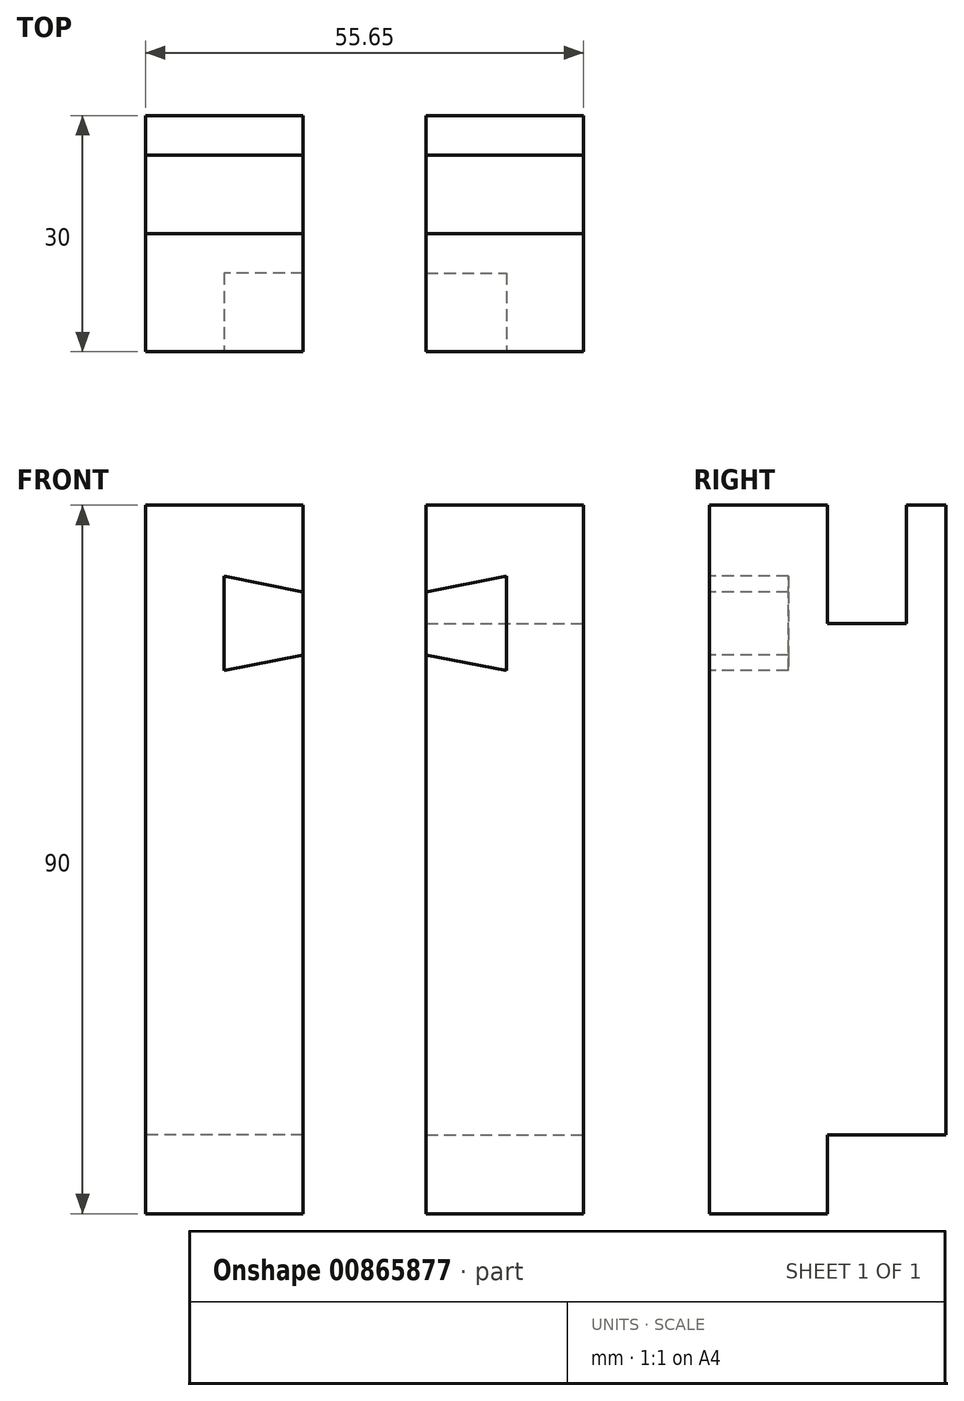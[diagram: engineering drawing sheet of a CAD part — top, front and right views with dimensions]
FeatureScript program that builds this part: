
annotation { "Feature Type Name" : "Feature", "Feature Type Description" : "" }
export const myFeature = defineFeature(function(context is Context, id is Id, definition is map)
    precondition{}
    {
        {
            var Q0;
            Q0=qCreatedBy(makeId("Top.planeOp"),FACE);
            var sketch = newSketch(context, id + "F0", { "sketchPlane" : qUnion([Q0])});
            skLineSegment(sketch, "E0.bottom", {"start": v(0, 0) * mm, "end": v(-20, 0) * mm});
            skLineSegment(sketch, "E0.top", {"start": v(0, 30) * mm, "end": v(-20, 30) * mm});
            skLineSegment(sketch, "E0.left", {"start": v(0, 0) * mm, "end": v(0, 30) * mm});
            skLineSegment(sketch, "E0.right", {"start": v(-20, 0) * mm, "end": v(-20, 30) * mm});
            skSolve(sketch);
        }
        {
            var Q0;
            Q0 = qSketchRegion(id + "F0", true);
            extrude(context, id + "F1", {"entities" : qUnion([Q0]), "depth" : 90 * mm, "offsetDistance" : 25 * mm});
        }
        {
            var Q0;
            Q0=makeQuery(id+"F1.opExtrude","CAP_FACE",FACE,{"disambiguationData":[OSD([sQuery(id+"F0.wireOp",EDGE,"E0.bottom"),sQuery(id+"F0.wireOp",EDGE,"E0.top"),sQuery(id+"F0.wireOp",EDGE,"E0.left"),sQuery(id+"F0.wireOp",EDGE,"E0.right")])],"isStart":false});
            var sketch = newSketch(context, id + "F2", { "sketchPlane" : qUnion([Q0])});
            skLineSegment(sketch, "E1.bottom", {"start": v(0, 15) * mm, "end": v(-20, 15) * mm});
            skLineSegment(sketch, "E1.top", {"start": v(0, 25) * mm, "end": v(-20, 25) * mm});
            skLineSegment(sketch, "E1.left", {"start": v(0, 15) * mm, "end": v(0, 25) * mm});
            skLineSegment(sketch, "E1.right", {"start": v(-20, 15) * mm, "end": v(-20, 25) * mm});
            skSolve(sketch);
        }
        {
            var Q0;
            Q0 = qSketchRegion(id + "F2", true);
            extrude(context, id + "F3", {"entities" : qUnion([Q0]), "operationType" : NewBodyOperationType.REMOVE, "oppositeDirection" : true, "depth" : 15 * mm, "offsetDistance" : 25 * mm});
        }
        {
            var Q0;
            Q0=makeQuery(id+"F1.opExtrude","CAP_FACE",FACE,{"disambiguationData":[OSD([sQuery(id+"F0.wireOp",EDGE,"E0.bottom"),sQuery(id+"F0.wireOp",EDGE,"E0.top"),sQuery(id+"F0.wireOp",EDGE,"E0.left"),sQuery(id+"F0.wireOp",EDGE,"E0.right")])],"isStart":true});
            var sketch = newSketch(context, id + "F4", { "sketchPlane" : qUnion([Q0])});
            skLineSegment(sketch, "E2.bottom", {"start": v(0, -30) * mm, "end": v(-20, -30) * mm});
            skLineSegment(sketch, "E2.top", {"start": v(0, -15) * mm, "end": v(-20, -15) * mm});
            skLineSegment(sketch, "E2.left", {"start": v(0, -30) * mm, "end": v(0, -15) * mm});
            skLineSegment(sketch, "E2.right", {"start": v(-20, -30) * mm, "end": v(-20, -15) * mm});
            skSolve(sketch);
        }
        {
            var Q0;
            Q0 = qSketchRegion(id + "F4", true);
            extrude(context, id + "F5", {"entities" : qUnion([Q0]), "operationType" : NewBodyOperationType.REMOVE, "oppositeDirection" : true, "depth" : 10 * mm, "offsetDistance" : 25 * mm});
        }
        {
            var Q0;
            Q0=makeQuery(id+"F1.opExtrude","SWEPT_FACE",FACE,{"disambiguationData":[OSD([sQuery(id+"F0.wireOp",EDGE,"E0.bottom")])]});
            var sketch = newSketch(context, id + "F6", { "sketchPlane" : qUnion([Q0])});
            skLineSegment(sketch, "E3", {"start": v(0, 79) * mm, "end": v(-10, 81) * mm});
            skLineSegment(sketch, "E4", {"start": v(-10, 81) * mm, "end": v(-10, 69) * mm});
            skLineSegment(sketch, "E5", {"start": v(-10, 69) * mm, "end": v(0, 71) * mm});
            skLineSegment(sketch, "E6", {"start": v(0, 71) * mm, "end": v(0, 79) * mm});
            skSolve(sketch);
        }
        {
            var Q0;
            Q0 = qSketchRegion(id + "F6", true);
            extrude(context, id + "F7", {"entities" : qUnion([Q0]), "operationType" : NewBodyOperationType.REMOVE, "oppositeDirection" : true, "depth" : 10 * mm, "offsetDistance" : 25 * mm});
        }
        {
            var Q0;
            Q0=qCreatedBy(makeId("Top.planeOp"),FACE);
            var sketch = newSketch(context, id + "F8", { "sketchPlane" : qUnion([Q0])});
            skLineSegment(sketch, "E7.bottom", {"start": v(15.65, 0) * mm, "end": v(35.65, 0) * mm});
            skLineSegment(sketch, "E7.top", {"start": v(15.65, 30) * mm, "end": v(35.65, 30) * mm});
            skLineSegment(sketch, "E7.left", {"start": v(15.65, 0) * mm, "end": v(15.65, 30) * mm});
            skLineSegment(sketch, "E7.right", {"start": v(35.65, 0) * mm, "end": v(35.65, 30) * mm});
            skSolve(sketch);
        }
        {
            var Q0;
            Q0 = qSketchRegion(id + "F8", true);
            extrude(context, id + "F9", {"entities" : qUnion([Q0]), "depth" : 90 * mm, "offsetDistance" : 25 * mm});
        }
        {
            var Q0;
            Q0=makeQuery(id+"F9.opExtrude","SWEPT_FACE",FACE,{"disambiguationData":[OSD([sQuery(id+"F8.wireOp",EDGE,"E7.right")])]});
            var sketch = newSketch(context, id + "F10", { "sketchPlane" : qUnion([Q0])});
            skLineSegment(sketch, "E8.bottom", {"start": v(15, 90) * mm, "end": v(25, 90) * mm});
            skLineSegment(sketch, "E8.top", {"start": v(15, 75) * mm, "end": v(25, 75) * mm});
            skLineSegment(sketch, "E8.left", {"start": v(15, 90) * mm, "end": v(15, 75) * mm});
            skLineSegment(sketch, "E8.right", {"start": v(25, 90) * mm, "end": v(25, 75) * mm});
            skLineSegment(sketch, "E9.bottom", {"start": v(30, 0) * mm, "end": v(15, 0) * mm});
            skLineSegment(sketch, "E9.top", {"start": v(30, 10) * mm, "end": v(15, 10) * mm});
            skLineSegment(sketch, "E9.left", {"start": v(30, 0) * mm, "end": v(30, 10) * mm});
            skLineSegment(sketch, "E9.right", {"start": v(15, 0) * mm, "end": v(15, 10) * mm});
            skSolve(sketch);
        }
        {
            var Q0;
            Q0 = qSketchRegion(id + "F10", true);
            extrude(context, id + "F11", {"entities" : qUnion([Q0]), "operationType" : NewBodyOperationType.REMOVE, "endBound" : BoundingType.THROUGH_ALL, "oppositeDirection" : true, "depth" : 25 * mm, "offsetDistance" : 25 * mm});
        }
        {
            var Q0;
            Q0=makeQuery(id+"F9.opExtrude","SWEPT_FACE",FACE,{"disambiguationData":[OSD([sQuery(id+"F8.wireOp",EDGE,"E7.bottom")])]});
            var sketch = newSketch(context, id + "F12", { "sketchPlane" : qUnion([Q0])});
            skLineSegment(sketch, "E10", {"start": v(15.65, 71) * mm, "end": v(25.83, 69) * mm});
            skLineSegment(sketch, "E11", {"start": v(25.83, 69) * mm, "end": v(25.83, 81) * mm});
            skLineSegment(sketch, "E12", {"start": v(25.83, 81) * mm, "end": v(15.65, 79) * mm});
            skLineSegment(sketch, "E13", {"start": v(15.65, 79) * mm, "end": v(15.65, 71) * mm});
            skSolve(sketch);
        }
        {
            var Q0;
            Q0 = qSketchRegion(id + "F12", true);
            extrude(context, id + "F13", {"entities" : qUnion([Q0]), "operationType" : NewBodyOperationType.REMOVE, "oppositeDirection" : true, "depth" : 10 * mm, "offsetDistance" : 25 * mm});
        }
    });
